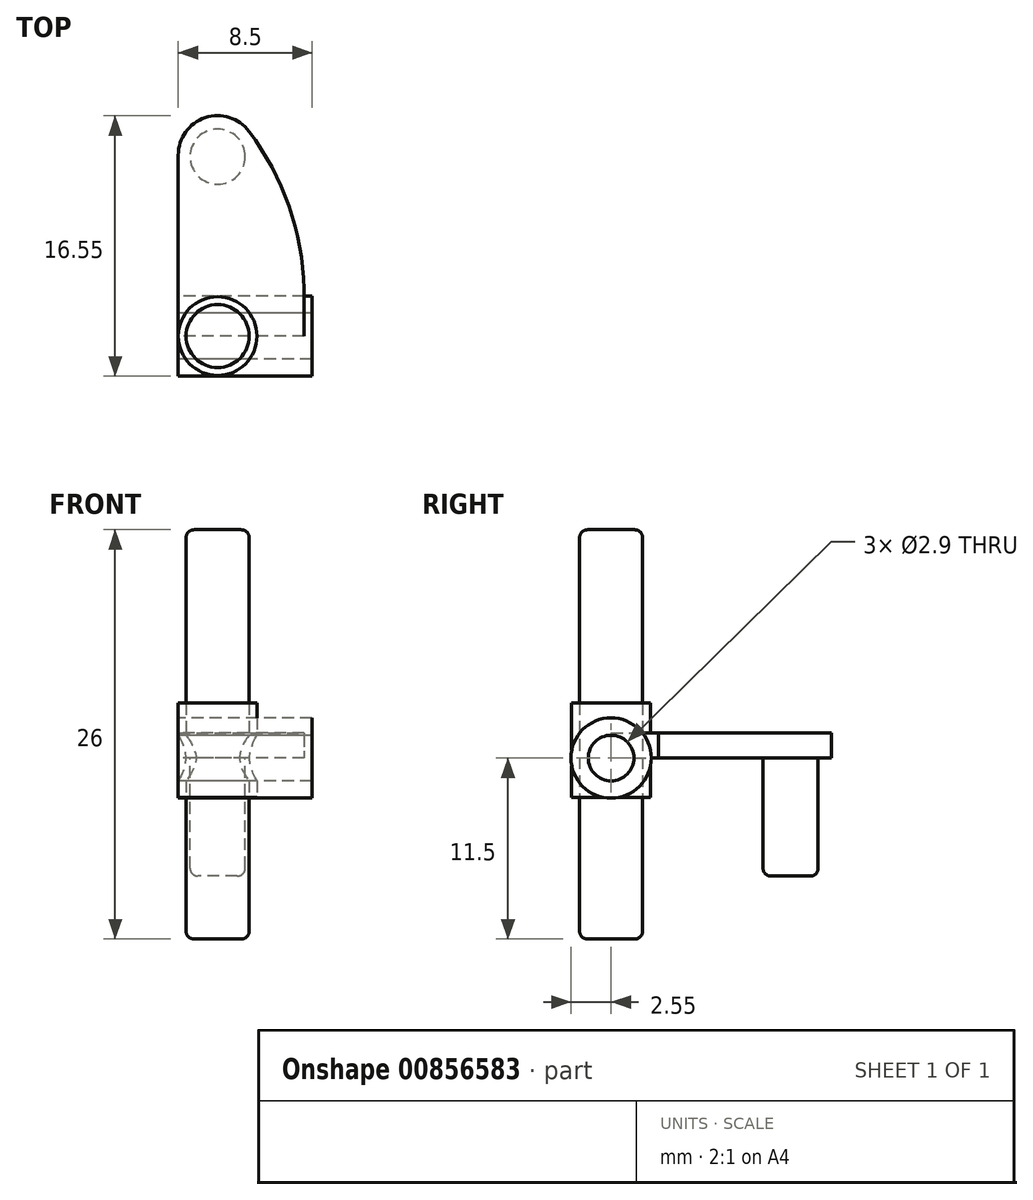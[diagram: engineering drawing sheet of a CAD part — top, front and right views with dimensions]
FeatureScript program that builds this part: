
annotation { "Feature Type Name" : "Feature", "Feature Type Description" : "" }
export const myFeature = defineFeature(function(context is Context, id is Id, definition is map)
    precondition{}
    {
        {
            var Q0;
            Q0=qCreatedBy(makeId("Right.planeOp"),FACE);
            var sketch = newSketch(context, id + "F0", { "sketchPlane" : qUnion([Q0])});
            skCircle(sketch, "E0", {"center": v(0, 0) * mm, "radius": 2.55 * mm});
            skSolve(sketch);
        }
        {
            var Q0;
            Q0 = qSketchRegion(id + "F0", true);
            extrude(context, id + "F1", {"entities" : qUnion([Q0]), "depth" : 8.5 * mm, "offsetDistance" : 25.4 * mm});
        }
        {
            var Q0;
            Q0=qCreatedBy(makeId("Top.planeOp"),FACE);
            var sketch = newSketch(context, id + "F2", { "sketchPlane" : qUnion([Q0])});
            skLineSegment(sketch, "E1", {"start": v(0, 0) * mm, "end": v(0, 11.5) * mm});
            skArc(sketch, "E2", {"start": v(0, 11.5) * mm, "mid": v(1.7, 13.87) * mm, "end": v(4.5, 13) * mm});
            skLineSegment(sketch, "E3", {"start": v(0, 0) * mm, "end": v(8, 0) * mm});
            skLineSegment(sketch, "E4", {"start": v(8, 0) * mm, "end": v(8, 3) * mm});
            skArc(sketch, "E5", {"start": v(4.5, 13) * mm, "mid": v(7.02, 8.27) * mm, "end": v(8, 3) * mm});
            skSolve(sketch);
        }
        {
            var Q0;
            Q0 = qSketchRegion(id + "F2", true);
            extrude(context, id + "F3", {"entities" : qUnion([Q0]), "depth" : 1.6 * mm, "offsetDistance" : 25.4 * mm});
        }
        {
            var Q0;
            Q0 = qSketchRegion(id + "F2", true);
            extrude(context, id + "F4", {"entities" : qUnion([Q0]), "depth" : 1.6 * mm, "offsetDistance" : 25.4 * mm});
        }
        {
            var Q0;
            Q0=qCreatedBy(makeId("Top.planeOp"),FACE);
            var sketch = newSketch(context, id + "F5", { "sketchPlane" : qUnion([Q0])});
            skCircle(sketch, "E6", {"center": v(2.5, 11.4) * mm, "radius": 1.75 * mm});
            skSolve(sketch);
        }
        {
            var Q0;
            Q0 = qSketchRegion(id + "F5", true);
            extrude(context, id + "F6", {"entities" : qUnion([Q0]), "oppositeDirection" : true, "depth" : 7.5 * mm, "offsetDistance" : 25.4 * mm});
        }
        {
            var Q0;
            Q0=qCreatedBy(makeId("Top.planeOp"),FACE);
            var sketch = newSketch(context, id + "F7", { "sketchPlane" : qUnion([Q0])});
            skCircle(sketch, "E7", {"center": v(2.5, 0) * mm, "radius": 2.5 * mm});
            skSolve(sketch);
        }
        {
            var Q0;
            Q0 = qSketchRegion(id + "F7", true);
            extrude(context, id + "F8", {"entities" : qUnion([Q0]), "depth" : 3.5 * mm, "offsetDistance" : 25.4 * mm, "hasSecondDirection" : true, "secondDirectionOppositeDirection" : true, "secondDirectionDepth" : 2.5 * mm});
        }
        {
            var Q0;
            Q0=qCreatedBy(makeId("Top.planeOp"),FACE);
            var sketch = newSketch(context, id + "F9", { "sketchPlane" : qUnion([Q0])});
            skCircle(sketch, "E8", {"center": v(2.5, 0) * mm, "radius": 2 * mm});
            skSolve(sketch);
        }
        {
            var Q0;
            Q0 = qSketchRegion(id + "F9", true);
            extrude(context, id + "F10", {"entities" : qUnion([Q0]), "depth" : 14.5 * mm, "offsetDistance" : 25.4 * mm, "hasSecondDirection" : true, "secondDirectionOppositeDirection" : true, "secondDirectionDepth" : 11.5 * mm});
        }
        {
            var Q0;
            Q0=sQuery(id+"F0.wireOp",VERTEX,"E0.center");
            var Q1;
            Q1=makeQuery(id+"F1.opExtrude","SWEPT_BODY",BODY,{"disambiguationData":[OSD([sQuery(id+"F0.wireOp",EDGE,"E0")])]});
            var Q2;
            Q2=makeQuery(id+"F3.opExtrude","SWEPT_BODY",BODY,{"disambiguationData":[OSD([sQuery(id+"F2.wireOp",EDGE,"E1"),sQuery(id+"F2.wireOp",EDGE,"E2"),sQuery(id+"F2.wireOp",EDGE,"E3"),sQuery(id+"F2.wireOp",EDGE,"E4"),sQuery(id+"F2.wireOp",EDGE,"E5")])]});
            var Q3;
            Q3=makeQuery(id+"F4.opExtrude","SWEPT_BODY",BODY,{"disambiguationData":[OSD([sQuery(id+"F2.wireOp",EDGE,"E1"),sQuery(id+"F2.wireOp",EDGE,"E2"),sQuery(id+"F2.wireOp",EDGE,"E3"),sQuery(id+"F2.wireOp",EDGE,"E4"),sQuery(id+"F2.wireOp",EDGE,"E5")])]});
            var Q4;
            Q4=makeQuery(id+"F8.opExtrude","SWEPT_BODY",BODY,{"disambiguationData":[OSD([sQuery(id+"F7.wireOp",EDGE,"E7")])]});
            var Q5;
            Q5=makeQuery(id+"F10.opExtrude","SWEPT_BODY",BODY,{"disambiguationData":[OSD([sQuery(id+"F9.wireOp",EDGE,"E8")])]});
            hole(context, id + "F11", {"style" : HoleStyle.SIMPLE, "endStyle" : HoleEndStyle.THROUGH, "oppositeDirection" : true, "holeDiameter" : 2.9 * mm, "majorDiameter" : 6.35 * mm, "isTappedThrough" : true, "tappedDepth" : 12.7 * mm, "tapClearance" : 3, "locations" : qUnion([Q0]), "scope" : qUnion([Q1, Q2, Q3, Q4, Q5])});
        }
        {
            var Q0;
            Q0=makeQuery(id+"F10.opExtrude","CAP_EDGE",EDGE,{"disambiguationData":[OSD([sQuery(id+"F9.wireOp",EDGE,"E8")])],"isStart":false});
            var Q1;
            Q1=makeQuery(id+"F10.opExtrude","CAP_EDGE",EDGE,{"disambiguationData":[OSD([sQuery(id+"F9.wireOp",EDGE,"E8")])],"isStart":true});
            var Q2;
            Q2=makeQuery(id+"F6.opExtrude","CAP_EDGE",EDGE,{"disambiguationData":[OSD([sQuery(id+"F5.wireOp",EDGE,"E6")])],"isStart":false});
            fillet(context, id + "F12", {"entities" : qUnion([Q0, Q1, Q2]), "radius" : 0.5 * mm, "tangentPropagation" : true, "allowEdgeOverflow" : false});
        }
    });
